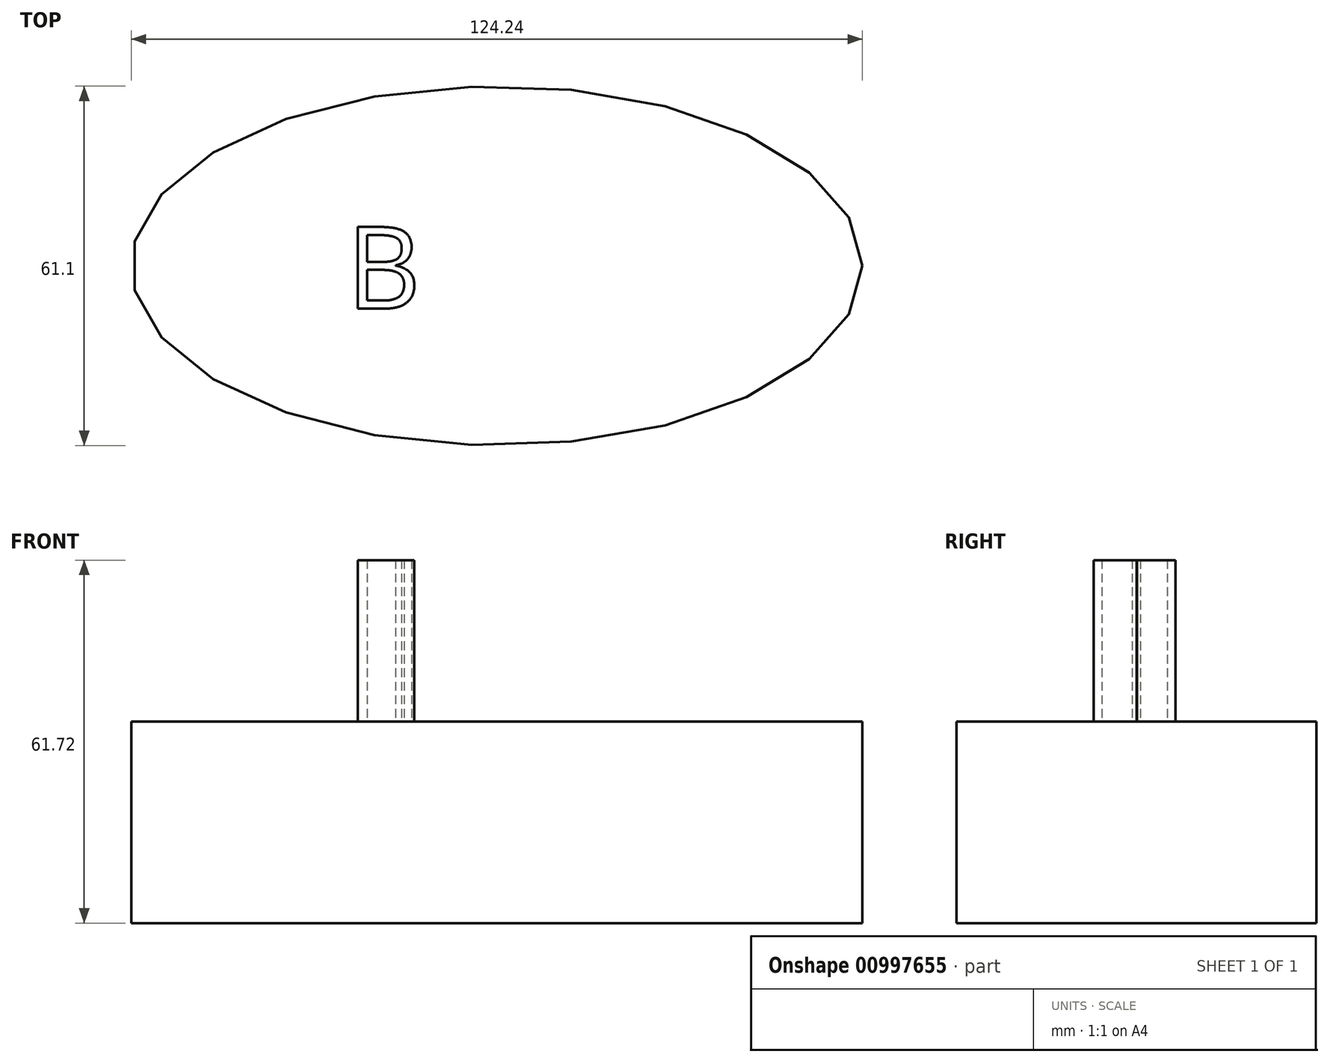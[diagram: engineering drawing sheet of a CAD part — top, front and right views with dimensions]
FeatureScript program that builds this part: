
annotation { "Feature Type Name" : "Feature", "Feature Type Description" : "" }
export const myFeature = defineFeature(function(context is Context, id is Id, definition is map)
    precondition{}
    {
        {
            var Q0;
            Q0=qCreatedBy(makeId("Top.planeOp"),FACE);
            var sketch = newSketch(context, id + "F0", { "sketchPlane" : qUnion([Q0])});
            skEllipse(sketch, "E0", {"center": v(0, 0) * mm, "majorRadius": 62.12 * mm, "minorRadius": 30.55 * mm, "majorAxis": v(1, 0)});
            skSolve(sketch);
        }
        {
            var Q0;
            Q0=makeQuery(id+"F0.imprint","IMPRINT",FACE,{"disambiguationData":[TD([[makeQuery(id+"F0.imprint","IMPRINT",EDGE,{"derivedFrom":sQuery(id+"F0.wireOp",EDGE,"E0")}),1.0]])]});
            extrude(context, id + "F1", {"entities" : qUnion([Q0]), "depth" : 34.3 * mm, "offsetDistance" : 25.4 * mm});
        }
        {
            var Q0;
            Q0=makeQuery(id+"F1.opExtrude","CAP_FACE",FACE,{"disambiguationData":[OSD([sQuery(id+"F0.wireOp",EDGE,"E0")])],"isStart":false});
            var sketch = newSketch(context, id + "F2", { "sketchPlane" : qUnion([Q0])});
            skText(sketch, "E1", { "text": "B", "fontName": "OpenSans-Regular.ttf"});
            const initialGuessF2  = {"E1": [-0.02556, -0.00727, 1, 0, 0.014]};
            skSetInitialGuess(sketch, initialGuessF2);
            skSolve(sketch);
        }
        {
            var Q0;
            Q0 = qSketchRegion(id + "F2", true);
            extrude(context, id + "F3", {"entities" : qUnion([Q0]), "operationType" : NewBodyOperationType.ADD, "depth" : 27.43 * mm, "offsetDistance" : 25.4 * mm});
        }
    });
